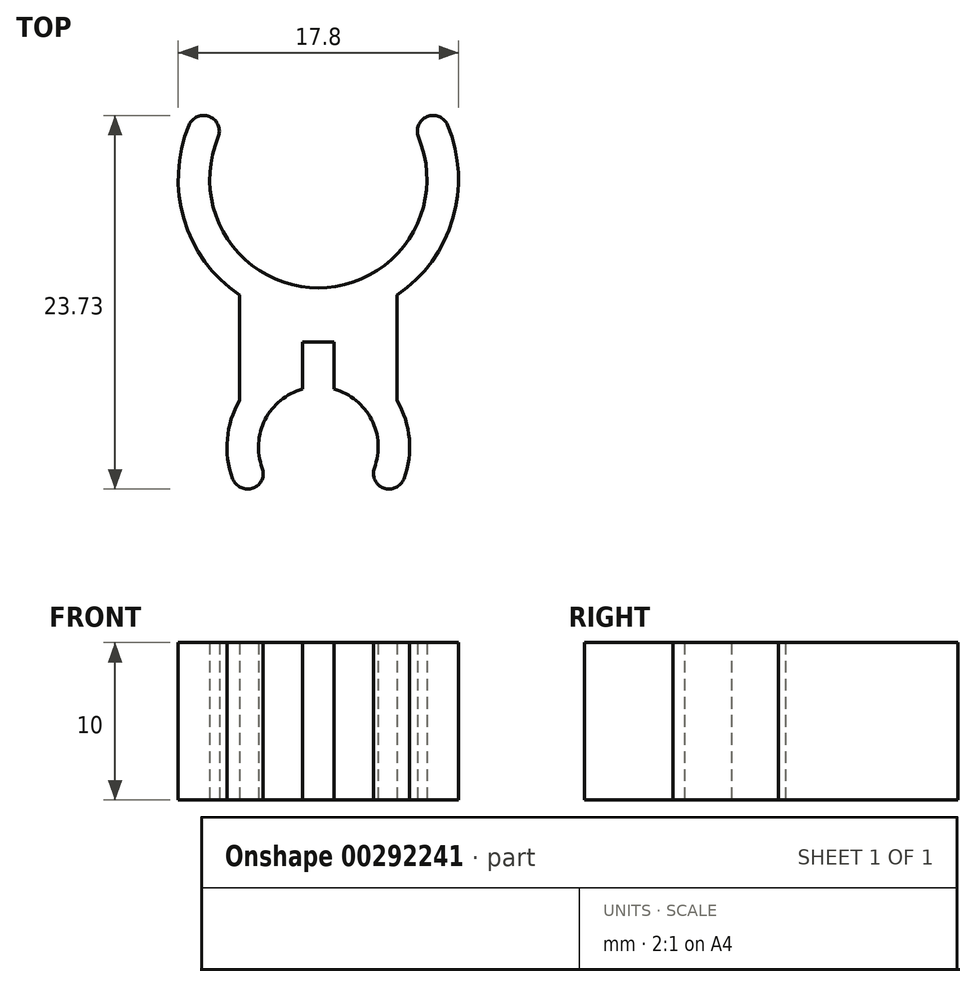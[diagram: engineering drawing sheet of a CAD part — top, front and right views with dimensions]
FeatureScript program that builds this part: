
annotation { "Feature Type Name" : "Feature", "Feature Type Description" : "" }
export const myFeature = defineFeature(function(context is Context, id is Id, definition is map)
    precondition{}
    {
        {
            var Q0;
            Q0=qCreatedBy(makeId("Top.planeOp"),FACE);
            var sketch = newSketch(context, id + "F0", { "sketchPlane" : qUnion([Q0])});
            skCircle(sketch, "E0", {"center": v(0, 0) * mm, "radius": 6.9 * mm});
            skCircle(sketch, "E1.0", {"center": v(0, 0) * mm, "radius": 8.9 * mm});
            skPoint(sketch, "E2", {"position": v(-5, -7.36) * mm});
            skPoint(sketch, "E3", {"position": v(5, -7.36) * mm});
            skPoint(sketch, "E4", {"position": v(0, -17) * mm});
            skCircle(sketch, "E5", {"center": v(0, -17) * mm, "radius": 3.8 * mm});
            skCircle(sketch, "E6.0", {"center": v(0, -17) * mm, "radius": 5.8 * mm});
            skLineSegment(sketch, "E7", {"start": v(-5, -7.36) * mm, "end": v(-5, -14.06) * mm});
            skLineSegment(sketch, "E8", {"start": v(5, -7.36) * mm, "end": v(5, -14.06) * mm});
            skPoint(sketch, "E9", {"position": v(-7.7, 4.45) * mm});
            skPoint(sketch, "E10", {"position": v(7.7, 4.45) * mm});
            skLineSegment(sketch, "E11", {"start": v(-7.7, 4.45) * mm, "end": v(0, 0) * mm});
            skLineSegment(sketch, "E12", {"start": v(0, 0) * mm, "end": v(7.7, 4.45) * mm});
            skPoint(sketch, "E13", {"position": v(-5.98, 3.45) * mm});
            skPoint(sketch, "E14", {"position": v(5.98, 3.45) * mm});
            skPoint(sketch, "E15", {"position": v(-4.9, -20.12) * mm});
            skPoint(sketch, "E16", {"position": v(4.9, -20.12) * mm});
            skLineSegment(sketch, "E17", {"start": v(-4.9, -20.12) * mm, "end": v(0, -17) * mm});
            skLineSegment(sketch, "E18", {"start": v(4.9, -20.12) * mm, "end": v(0, -17) * mm});
            skPoint(sketch, "E19", {"position": v(-1, -13.33) * mm});
            skPoint(sketch, "E20", {"position": v(1, -13.33) * mm});
            skLineSegment(sketch, "E21.bottom", {"start": v(-1, -13.33) * mm, "end": v(1, -13.33) * mm});
            skLineSegment(sketch, "E21.top", {"start": v(-1, -10.33) * mm, "end": v(1, -10.33) * mm});
            skLineSegment(sketch, "E21.left", {"start": v(-1, -13.33) * mm, "end": v(-1, -10.33) * mm});
            skLineSegment(sketch, "E21.right", {"start": v(1, -13.33) * mm, "end": v(1, -10.33) * mm});
            skSolve(sketch);
        }
        {
            var Q0;
            {var subQ5=sQuery(id+"F0.wireOp",EDGE,"E11");var subQ7=sQuery(id+"F0.wireOp",EDGE,"E0");var subQ8=makeQuery(id+"F0.imprint","INTERSECT",VERTEX,{"derivedFrom":[subQ7,subQ5]});Q0=makeQuery(id+"F0.imprint","IMPRINT",FACE,{"disambiguationData":[TD([[makeQuery(id+"F0.imprint","IMPRINT",EDGE,{"disambiguationData":[TD([[subQ8,-1.0]])],"derivedFrom":subQ7}),-1.0]])]});}
            var Q1;
            {var subQ0=sQuery(id+"F0.wireOp",EDGE,"E7");Q1=makeQuery(id+"F0.imprint","IMPRINT",FACE,{"disambiguationData":[TD([[makeQuery(id+"F0.imprint","IMPRINT",EDGE,{"derivedFrom":subQ0}),1.0]])]});}
            var Q2;
            {var subQ0=sQuery(id+"F0.wireOp",EDGE,"E6.0");var subQ1=makeQuery(id+"F0.imprint","INTERSECT",VERTEX,{"derivedFrom":[subQ0,sQuery(id+"F0.wireOp",EDGE,"E7")]});Q2=makeQuery(id+"F0.imprint","IMPRINT",FACE,{"disambiguationData":[TD([[makeQuery(id+"F0.imprint","IMPRINT",EDGE,{"disambiguationData":[TD([[subQ1,1.0]])],"derivedFrom":subQ0}),1.0]])]});}
            var Q3;
            {var subQ0=sQuery(id+"F0.wireOp",EDGE,"E6.0");var subQ1=makeQuery(id+"F0.imprint","INTERSECT",VERTEX,{"derivedFrom":[subQ0,sQuery(id+"F0.wireOp",EDGE,"E8")]});Q3=makeQuery(id+"F0.imprint","IMPRINT",FACE,{"disambiguationData":[TD([[makeQuery(id+"F0.imprint","IMPRINT",EDGE,{"disambiguationData":[TD([[subQ1,-1.0]])],"derivedFrom":subQ0}),1.0]])]});}
            extrude(context, id + "F1", {"entities" : qUnion([Q0, Q1, Q2, Q3]), "depth" : 10 * mm});
        }
        {
            var Q0;
            Q0=makeQuery(id+"F1.opExtrude","SWEPT_EDGE",EDGE,{"disambiguationData":[OSD([sQuery(id+"F0.wireOp",EDGE,"E1.0"),sQuery(id+"F0.wireOp",EDGE,"E11")])]});
            var Q1;
            Q1=makeQuery(id+"F1.opExtrude","SWEPT_EDGE",EDGE,{"disambiguationData":[OSD([sQuery(id+"F0.wireOp",EDGE,"E0"),sQuery(id+"F0.wireOp",EDGE,"E11")])]});
            var Q2;
            Q2=makeQuery(id+"F1.opExtrude","SWEPT_EDGE",EDGE,{"disambiguationData":[OSD([sQuery(id+"F0.wireOp",EDGE,"E0"),sQuery(id+"F0.wireOp",EDGE,"E12")])]});
            var Q3;
            Q3=makeQuery(id+"F1.opExtrude","SWEPT_EDGE",EDGE,{"disambiguationData":[OSD([sQuery(id+"F0.wireOp",EDGE,"E1.0"),sQuery(id+"F0.wireOp",EDGE,"E12")])]});
            var Q4;
            Q4=makeQuery(id+"F1.opExtrude","SWEPT_EDGE",EDGE,{"disambiguationData":[OSD([sQuery(id+"F0.wireOp",EDGE,"E6.0"),sQuery(id+"F0.wireOp",EDGE,"E17")])]});
            var Q5;
            Q5=makeQuery(id+"F1.opExtrude","SWEPT_EDGE",EDGE,{"disambiguationData":[OSD([sQuery(id+"F0.wireOp",EDGE,"E5"),sQuery(id+"F0.wireOp",EDGE,"E17")])]});
            var Q6;
            Q6=makeQuery(id+"F1.opExtrude","SWEPT_EDGE",EDGE,{"disambiguationData":[OSD([sQuery(id+"F0.wireOp",EDGE,"E6.0"),sQuery(id+"F0.wireOp",EDGE,"E18")])]});
            var Q7;
            Q7=makeQuery(id+"F1.opExtrude","SWEPT_EDGE",EDGE,{"disambiguationData":[OSD([sQuery(id+"F0.wireOp",EDGE,"E5"),sQuery(id+"F0.wireOp",EDGE,"E18")])]});
            fillet(context, id + "F2", {"entities" : qUnion([Q0, Q1, Q2, Q3, Q4, Q5, Q6, Q7]), "radius" : 1 * mm, "tangentPropagation" : true, "allowEdgeOverflow" : false});
        }
    });
